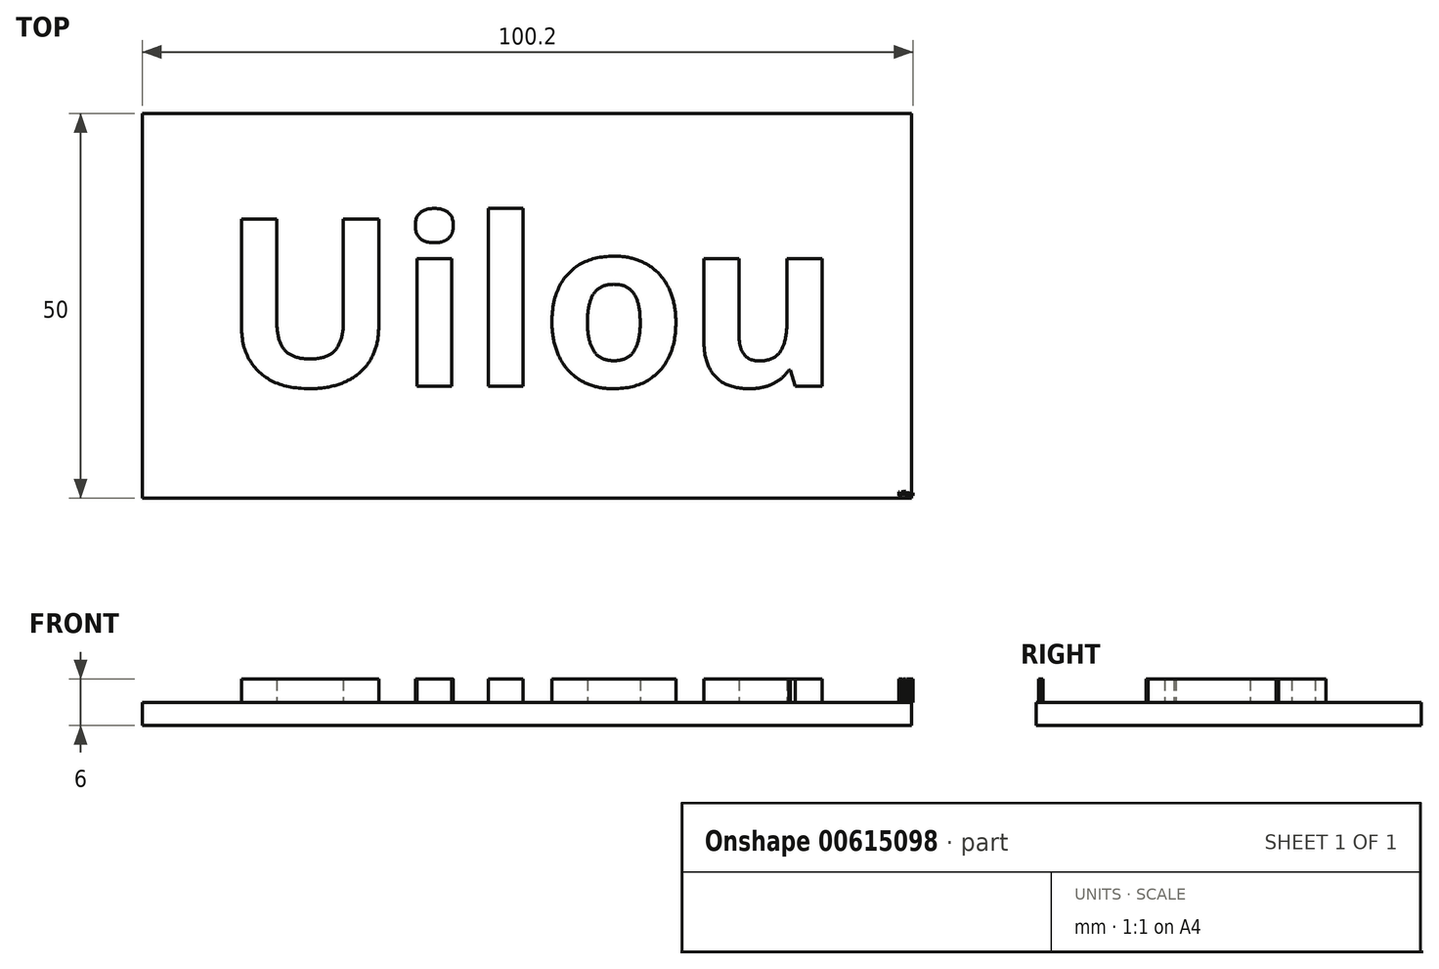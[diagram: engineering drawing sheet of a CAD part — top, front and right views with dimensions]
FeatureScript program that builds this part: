
annotation { "Feature Type Name" : "Feature", "Feature Type Description" : "" }
export const myFeature = defineFeature(function(context is Context, id is Id, definition is map)
    precondition{}
    {
        {
            var Q0;
            Q0=qCreatedBy(makeId("Top.planeOp"),FACE);
            var sketch = newSketch(context, id + "F0", { "sketchPlane" : qUnion([Q0])});
            skLineSegment(sketch, "E0.bottom", {"start": v(0, 0) * mm, "end": v(-100, 0) * mm});
            skLineSegment(sketch, "E0.top", {"start": v(0, 50) * mm, "end": v(-100, 50) * mm});
            skLineSegment(sketch, "E0.left", {"start": v(0, 0) * mm, "end": v(0, 50) * mm});
            skLineSegment(sketch, "E0.right", {"start": v(-100, 0) * mm, "end": v(-100, 50) * mm});
            skLineSegment(sketch, "E1.bottom", {"start": v(-50, 50) * mm, "end": v(-67.38, 50) * mm});
            skLineSegment(sketch, "E1.top", {"start": v(-50, 50) * mm, "end": v(-67.38, 50) * mm});
            skLineSegment(sketch, "E1.left", {"start": v(-50, 50) * mm, "end": v(-50, 50) * mm});
            skLineSegment(sketch, "E1.right", {"start": v(-67.38, 50) * mm, "end": v(-67.38, 50) * mm});
            skSolve(sketch);
        }
        {
            var Q0;
            Q0 = qSketchRegion(id + "F0", true);
            extrude(context, id + "F1", {"entities" : qUnion([Q0]), "depth" : 3 * mm, "offsetDistance" : 25 * mm});
        }
        {
            var Q0;
            Q0=makeQuery(id+"F1.opExtrude","CAP_FACE",FACE,{"disambiguationData":[OSD([sQuery(id+"F0.wireOp",EDGE,"E0.bottom"),sQuery(id+"F0.wireOp",EDGE,"E0.top"),sQuery(id+"F0.wireOp",EDGE,"E0.left"),sQuery(id+"F0.wireOp",EDGE,"E0.right"),sQuery(id+"F0.wireOp",EDGE,"E1.top")])],"isStart":false});
            var sketch = newSketch(context, id + "F2", { "sketchPlane" : qUnion([Q0])});
            skSolve(sketch);
        }
        {
            var Q0;
            Q0=makeQuery(id+"F2.imprint","IMPRINT",FACE,{"disambiguationData":[TD([[makeQuery(id+"F2.imprint","IMPRINT",EDGE,{"derivedFrom":makeQuery(id+"F1.opExtrude","CAP_EDGE",EDGE,{"disambiguationData":[OSD([sQuery(id+"F0.wireOp",EDGE,"E0.bottom")])],"isStart":false})}),-1.0]])]});
            var sketch = newSketch(context, id + "F3", { "sketchPlane" : qUnion([Q0])});
            skText(sketch, "E2", { "text": "Uilou", "fontName": "OpenSans-Bold.ttf"});
            skText(sketch, "E3", { "text": "Uilou", "fontName": "OpenSans-Bold.ttf"});
            const initialGuessF3  = {"E2": [-0.00176, 0.00031, 1, 0, 0.00055], "E3": [-0.08967, 0.01454, 1, 0, 0.0219]};
            skSetInitialGuess(sketch, initialGuessF3);
            skSolve(sketch);
        }
        {
            var Q0;
            Q0 = qSketchRegion(id + "F3", true);
            extrude(context, id + "F4", {"entities" : qUnion([Q0]), "operationType" : NewBodyOperationType.ADD, "depth" : 3 * mm, "offsetDistance" : 25 * mm});
        }
    });
